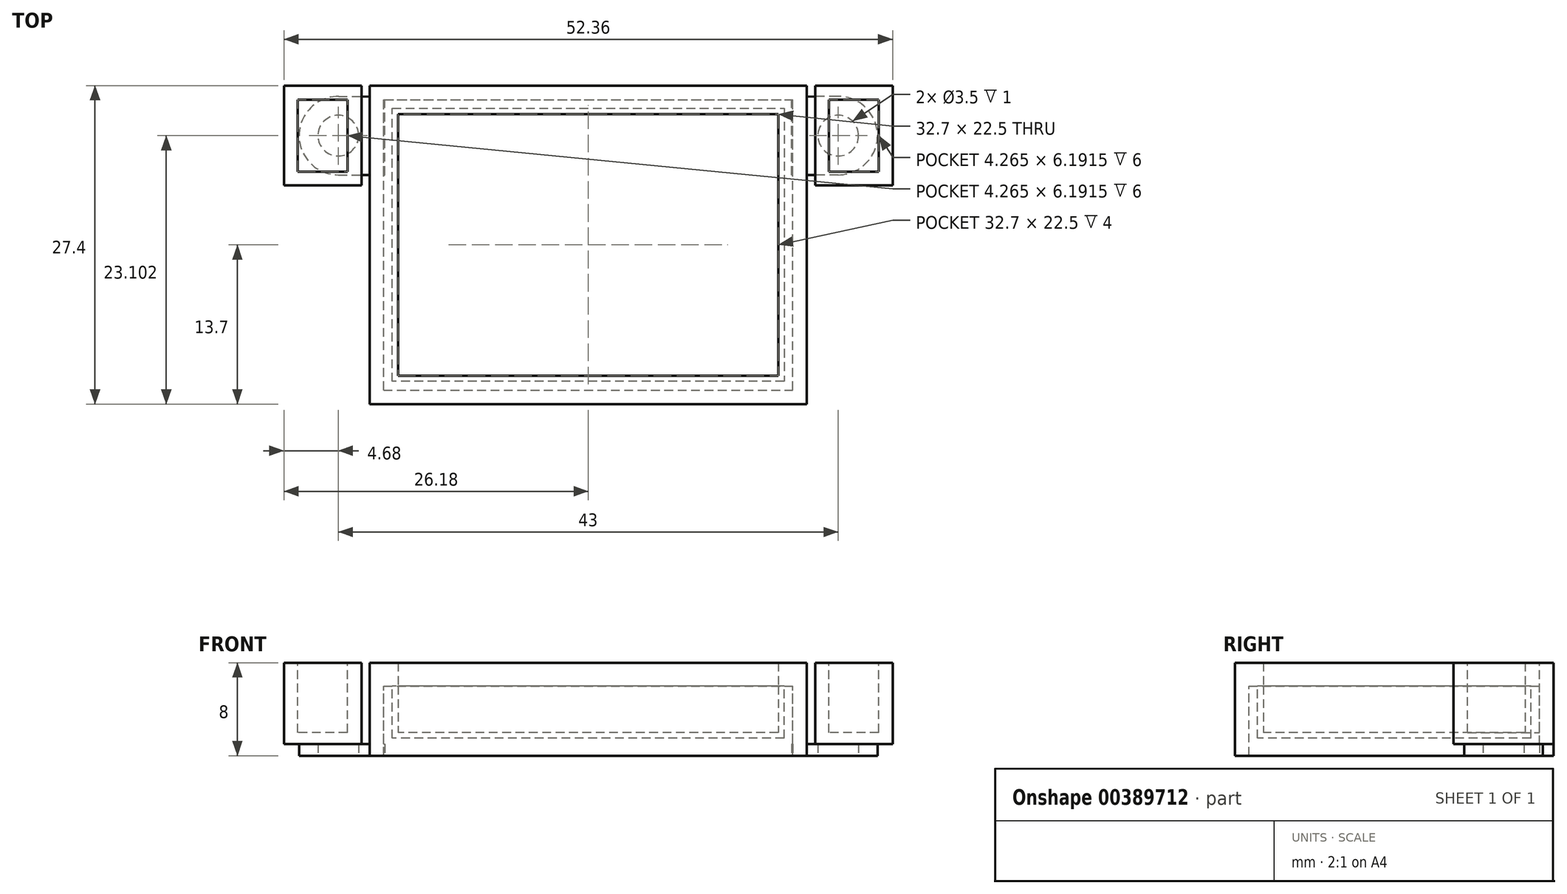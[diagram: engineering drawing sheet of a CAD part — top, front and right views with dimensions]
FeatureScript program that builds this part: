
annotation { "Feature Type Name" : "Feature", "Feature Type Description" : "" }
export const myFeature = defineFeature(function(context is Context, id is Id, definition is map)
    precondition{}
    {
        {
            var Q0;
            Q0=qCreatedBy(makeId("Top.planeOp"),FACE);
            var sketch = newSketch(context, id + "F0", { "sketchPlane" : qUnion([Q0])});
            skLineSegment(sketch, "E0.bottom", {"start": v(-15.2, 11.25) * mm, "end": v(-12.4, 11.25) * mm});
            skLineSegment(sketch, "E0.top", {"start": v(-15.2, -11.25) * mm, "end": v(-12.4, -11.25) * mm});
            skLineSegment(sketch, "E0.left", {"start": v(-15.2, 11.25) * mm, "end": v(-15.2, -11.25) * mm});
            skLineSegment(sketch, "E0.right", {"start": v(-12.4, 11.25) * mm, "end": v(-12.4, -11.25) * mm});
            skLineSegment(sketch, "E1", {"start": v(-42.25, 0) * mm, "end": v(42.25, 0) * mm, "construction": true});
            skLineSegment(sketch, "E2", {"start": v(0, 24.53) * mm, "end": v(0, -24.53) * mm, "construction": true});
            skLineSegment(sketch, "E3.MirrorCS", {"start": v(12.4, 11.25) * mm, "end": v(12.4, -11.25) * mm});
            skLineSegment(sketch, "E4.MirrorCS", {"start": v(15.2, -11.25) * mm, "end": v(12.4, -11.25) * mm});
            skLineSegment(sketch, "E5.MirrorCS", {"start": v(15.2, 11.25) * mm, "end": v(15.2, -11.25) * mm});
            skLineSegment(sketch, "E6.MirrorCS", {"start": v(15.2, 11.25) * mm, "end": v(12.4, 11.25) * mm});
            skLineSegment(sketch, "E7.bottom", {"start": v(-17.6, -12.5) * mm, "end": v(17.6, -12.5) * mm});
            skLineSegment(sketch, "E7.top", {"start": v(-17.6, 12.5) * mm, "end": v(17.6, 12.5) * mm});
            skLineSegment(sketch, "E7.left", {"start": v(-17.6, -12.5) * mm, "end": v(-17.6, 12.5) * mm});
            skLineSegment(sketch, "E7.right", {"start": v(17.6, -12.5) * mm, "end": v(17.6, 12.5) * mm});
            skLineSegment(sketch, "E8.0", {"start": v(-18.8, 13.7) * mm, "end": v(18.8, 13.7) * mm});
            skLineSegment(sketch, "E8.1", {"start": v(-18.8, -13.7) * mm, "end": v(-18.8, 13.7) * mm});
            skLineSegment(sketch, "E8.2", {"start": v(-18.8, -13.7) * mm, "end": v(18.8, -13.7) * mm});
            skLineSegment(sketch, "E8.3", {"start": v(18.8, -13.7) * mm, "end": v(18.8, 13.7) * mm});
            skLineSegment(sketch, "E9.bottom", {"start": v(-19.51, 13.7) * mm, "end": v(-26.18, 13.7) * mm});
            skLineSegment(sketch, "E9.top", {"start": v(-19.51, 5.1) * mm, "end": v(-26.18, 5.1) * mm});
            skLineSegment(sketch, "E9.left", {"start": v(-19.51, 13.7) * mm, "end": v(-19.51, 5.1) * mm});
            skLineSegment(sketch, "E9.right", {"start": v(-26.18, 13.7) * mm, "end": v(-26.18, 5.1) * mm});
            skLineSegment(sketch, "E10.MirrorCS", {"start": v(19.51, 13.7) * mm, "end": v(19.51, 5.1) * mm});
            skLineSegment(sketch, "E11.MirrorCS", {"start": v(19.51, 13.7) * mm, "end": v(26.18, 13.7) * mm});
            skLineSegment(sketch, "E12.MirrorCS", {"start": v(26.18, 13.7) * mm, "end": v(26.18, 5.1) * mm});
            skLineSegment(sketch, "E13.MirrorCS", {"start": v(19.51, 5.1) * mm, "end": v(26.18, 5.1) * mm});
            skSolve(sketch);
        }
        {
            var Q0;
            Q0 = qSketchRegion(id + "F0", true);
            var Q1;
            Q1=makeQuery(id+"F0.imprint","IMPRINT",FACE,{"disambiguationData":[TD([[makeQuery(id+"F0.imprint","IMPRINT",EDGE,{"derivedFrom":sQuery(id+"F0.wireOp",EDGE,"E0.bottom")}),1.0]])]});
            extrude(context, id + "F1", {"entities" : qUnion([Q0, Q1]), "depth" : 2 * mm});
        }
        {
            var Q0;
            Q0=makeQuery(id+"F0.imprint","IMPRINT",FACE,{"disambiguationData":[TD([[makeQuery(id+"F0.imprint","IMPRINT",EDGE,{"derivedFrom":sQuery(id+"F0.wireOp",EDGE,"E7.bottom")}),-1.0]])]});
            extrude(context, id + "F2", {"entities" : qUnion([Q0]), "operationType" : NewBodyOperationType.ADD, "oppositeDirection" : true, "depth" : 6 * mm});
        }
        {
            var Q0;
            Q0=makeQuery(id+"F2.opExtrude","CAP_FACE",FACE,{"disambiguationData":[OSD([sQuery(id+"F0.wireOp",EDGE,"E7.bottom"),sQuery(id+"F0.wireOp",EDGE,"E7.top"),sQuery(id+"F0.wireOp",EDGE,"E7.left"),sQuery(id+"F0.wireOp",EDGE,"E7.right"),sQuery(id+"F0.wireOp",EDGE,"E8.0"),sQuery(id+"F0.wireOp",EDGE,"E8.1"),sQuery(id+"F0.wireOp",EDGE,"E8.2"),sQuery(id+"F0.wireOp",EDGE,"E8.3")])],"isStart":false});
            var sketch = newSketch(context, id + "F3", { "sketchPlane" : qUnion([Q0])});
            skLineSegment(sketch, "E14.0", {"start": v(-17.5, -12.75) * mm, "end": v(17.5, -12.75) * mm, "construction": true});
            skCircle(sketch, "E15", {"center": v(-21.5, -9.4) * mm, "radius": 1.75 * mm});
            skLineSegment(sketch, "E16.0", {"start": v(-17.5, 12.25) * mm, "end": v(-17.5, -12.75) * mm});
            skLineSegment(sketch, "E17", {"start": v(-21.5, -6.03) * mm, "end": v(-17.5, -6.03) * mm});
            skLineSegment(sketch, "E18", {"start": v(-17.5, -6.03) * mm, "end": v(-17.5, -12.75) * mm});
            skLineSegment(sketch, "E19", {"start": v(-21.48, -12.78) * mm, "end": v(-17.5, -12.75) * mm});
            skArc(sketch, "E20", {"start": v(-21.5, -6.03) * mm, "mid": v(-24.87, -9.61) * mm, "end": v(-21.08, -12.75) * mm});
            skArc(sketch, "E21", {"start": v(-21.08, -12.75) * mm, "mid": v(-18.13, -9.2) * mm, "end": v(-21.5, -6.03) * mm, "construction": true});
            skLineSegment(sketch, "E22", {"start": v(0, -19.53) * mm, "end": v(0, 18.18) * mm, "construction": true});
            skPoint(sketch, "E22.endSnap0", {"position": v(0, -12.75) * mm});
            skLineSegment(sketch, "E23.MirrorCS", {"start": v(21.5, -6.03) * mm, "end": v(17.5, -6.03) * mm});
            skArc(sketch, "E24.MirrorCS", {"start": v(21.5, -6.03) * mm, "mid": v(24.87, -9.61) * mm, "end": v(21.08, -12.75) * mm});
            skLineSegment(sketch, "E25.MirrorCS", {"start": v(21.48, -12.78) * mm, "end": v(17.5, -12.75) * mm});
            skLineSegment(sketch, "E26.MirrorCS", {"start": v(17.5, -6.03) * mm, "end": v(17.5, -12.75) * mm});
            skCircle(sketch, "E27.MirrorC", {"center": v(21.5, -9.4) * mm, "radius": 1.75 * mm});
            skSolve(sketch);
        }
        {
            var Q0;
            Q0 = qSketchRegion(id + "F3", true);
            extrude(context, id + "F4", {"entities" : qUnion([Q0]), "operationType" : NewBodyOperationType.ADD, "oppositeDirection" : true, "depth" : 1 * mm});
        }
        {
            var Q0;
            Q0=makeQuery(id+"F1.opExtrude","CAP_FACE",FACE,{"disambiguationData":[OSD([sQuery(id+"F0.wireOp",EDGE,"E9.bottom"),sQuery(id+"F0.wireOp",EDGE,"E9.top"),sQuery(id+"F0.wireOp",EDGE,"E9.left"),sQuery(id+"F0.wireOp",EDGE,"E9.right")])],"isStart":true});
            var Q1;
            Q1=makeQuery(id+"F1.opExtrude","CAP_FACE",FACE,{"disambiguationData":[OSD([sQuery(id+"F0.wireOp",EDGE,"E10.MirrorCS"),sQuery(id+"F0.wireOp",EDGE,"E11.MirrorCS"),sQuery(id+"F0.wireOp",EDGE,"E12.MirrorCS"),sQuery(id+"F0.wireOp",EDGE,"E13.MirrorCS")])],"isStart":true});
            extrude(context, id + "F5", {"entities" : qUnion([Q0, Q1]), "operationType" : NewBodyOperationType.ADD, "depth" : 5 * mm});
        }
        {
            var Q0;
            Q0=makeQuery(id+"F1.opExtrude","CAP_FACE",FACE,{"disambiguationData":[OSD([sQuery(id+"F0.wireOp",EDGE,"E9.bottom"),sQuery(id+"F0.wireOp",EDGE,"E9.top"),sQuery(id+"F0.wireOp",EDGE,"E9.left"),sQuery(id+"F0.wireOp",EDGE,"E9.right")])],"isStart":false});
            var sketch = newSketch(context, id + "F6", { "sketchPlane" : qUnion([Q0])});
            skLineSegment(sketch, "E28.0.0", {"start": v(19.51, 13.7) * mm, "end": v(19.51, 5.1) * mm, "construction": true});
            skLineSegment(sketch, "E28.0.1", {"start": v(19.51, 5.1) * mm, "end": v(26.18, 5.1) * mm, "construction": true});
            skLineSegment(sketch, "E28.0.2", {"start": v(26.18, 5.1) * mm, "end": v(26.18, 13.7) * mm, "construction": true});
            skLineSegment(sketch, "E28.0.3", {"start": v(26.18, 13.7) * mm, "end": v(19.51, 13.7) * mm, "construction": true});
            skLineSegment(sketch, "E29.0", {"start": v(-19.51, 5.1) * mm, "end": v(-26.18, 5.1) * mm, "construction": true});
            skLineSegment(sketch, "E29.1", {"start": v(-26.18, 13.7) * mm, "end": v(-26.18, 5.1) * mm, "construction": true});
            skLineSegment(sketch, "E29.2", {"start": v(-19.51, 13.7) * mm, "end": v(-26.18, 13.7) * mm, "construction": true});
            skLineSegment(sketch, "E29.3", {"start": v(-19.51, 13.7) * mm, "end": v(-19.51, 5.1) * mm, "construction": true});
            skLineSegment(sketch, "E30.0", {"start": v(-20.71, 12.5) * mm, "end": v(-24.98, 12.5) * mm});
            skLineSegment(sketch, "E30.1", {"start": v(-20.71, 12.5) * mm, "end": v(-20.71, 6.3) * mm});
            skLineSegment(sketch, "E30.2", {"start": v(-20.71, 6.3) * mm, "end": v(-24.98, 6.3) * mm});
            skLineSegment(sketch, "E30.3", {"start": v(-24.98, 12.5) * mm, "end": v(-24.98, 6.3) * mm});
            skLineSegment(sketch, "E31.0", {"start": v(24.98, 12.5) * mm, "end": v(20.71, 12.5) * mm});
            skLineSegment(sketch, "E31.1", {"start": v(24.98, 6.3) * mm, "end": v(24.98, 12.5) * mm});
            skLineSegment(sketch, "E31.2", {"start": v(20.71, 6.3) * mm, "end": v(24.98, 6.3) * mm});
            skLineSegment(sketch, "E31.3", {"start": v(20.71, 12.5) * mm, "end": v(20.71, 6.3) * mm});
            skSolve(sketch);
        }
        {
            var Q0;
            Q0=makeQuery(id+"F6.imprint","IMPRINT",FACE,{"disambiguationData":[TD([[makeQuery(id+"F6.imprint","IMPRINT",EDGE,{"derivedFrom":sQuery(id+"F6.wireOp",EDGE,"E30.0")}),1.0]])]});
            var Q1;
            Q1=makeQuery(id+"F6.imprint","IMPRINT",FACE,{"disambiguationData":[TD([[makeQuery(id+"F6.imprint","IMPRINT",EDGE,{"derivedFrom":sQuery(id+"F6.wireOp",EDGE,"E31.0")}),1.0]])]});
            extrude(context, id + "F7", {"entities" : qUnion([Q0, Q1]), "operationType" : NewBodyOperationType.REMOVE, "oppositeDirection" : true, "depth" : 6 * mm});
        }
        {
            var Q0;
            Q0=makeQuery(id+"F1.opExtrude","CAP_FACE",FACE,{"disambiguationData":[OSD([sQuery(id+"F0.wireOp",EDGE,"E0.bottom"),sQuery(id+"F0.wireOp",EDGE,"E0.top"),sQuery(id+"F0.wireOp",EDGE,"E0.left"),sQuery(id+"F0.wireOp",EDGE,"E0.right"),sQuery(id+"F0.wireOp",EDGE,"E3.MirrorCS"),sQuery(id+"F0.wireOp",EDGE,"E4.MirrorCS"),sQuery(id+"F0.wireOp",EDGE,"E5.MirrorCS"),sQuery(id+"F0.wireOp",EDGE,"E6.MirrorCS"),sQuery(id+"F0.wireOp",EDGE,"E7.bottom"),sQuery(id+"F0.wireOp",EDGE,"E7.top"),sQuery(id+"F0.wireOp",EDGE,"E7.left"),sQuery(id+"F0.wireOp",EDGE,"E7.right")])],"isStart":true});
            cPlane(context, id + "F8", {"entities" : qUnion([Q0]), "cplaneType" : CPlaneType.OFFSET, "offset" : 0 * mm, "width" : 150 * mm, "height" : 150 * mm});
        }
        {
            var Q0;
            Q0=qCreatedBy(id+"F8.planeOp",FACE);
            var sketch = newSketch(context, id + "F9", { "sketchPlane" : qUnion([Q0])});
            skLineSegment(sketch, "E32.0.0", {"start": v(-17.6, -12.5) * mm, "end": v(17.6, -12.5) * mm});
            skLineSegment(sketch, "E32.0.1", {"start": v(17.6, -12.5) * mm, "end": v(17.6, 12.5) * mm});
            skLineSegment(sketch, "E32.0.2", {"start": v(17.6, 12.5) * mm, "end": v(-17.6, 12.5) * mm});
            skLineSegment(sketch, "E32.0.3", {"start": v(-17.6, 12.5) * mm, "end": v(-17.6, -12.5) * mm});
            skLineSegment(sketch, "E33.0", {"start": v(16.85, 11.75) * mm, "end": v(-16.85, 11.75) * mm});
            skLineSegment(sketch, "E33.1", {"start": v(16.85, -11.75) * mm, "end": v(16.85, 11.75) * mm});
            skLineSegment(sketch, "E33.2", {"start": v(-16.85, -11.75) * mm, "end": v(16.85, -11.75) * mm});
            skLineSegment(sketch, "E33.3", {"start": v(-16.85, 11.75) * mm, "end": v(-16.85, -11.75) * mm});
            skLineSegment(sketch, "E34.0", {"start": v(16.35, 11.25) * mm, "end": v(-16.35, 11.25) * mm});
            skLineSegment(sketch, "E34.1", {"start": v(16.35, -11.25) * mm, "end": v(16.35, 11.25) * mm});
            skLineSegment(sketch, "E34.2", {"start": v(-16.35, -11.25) * mm, "end": v(16.35, -11.25) * mm});
            skLineSegment(sketch, "E34.3", {"start": v(-16.35, 11.25) * mm, "end": v(-16.35, -11.25) * mm});
            skPoint(sketch, "E35.0", {"position": v(-17.6, -12.5) * mm});
            skPoint(sketch, "E35.1", {"position": v(-17.6, 12.5) * mm});
            skPoint(sketch, "E35.2", {"position": v(17.6, 12.5) * mm});
            skPoint(sketch, "E35.3", {"position": v(17.6, -12.5) * mm});
            skSolve(sketch);
        }
        {
            var Q0;
            Q0=makeQuery(id+"F9.imprint","IMPRINT",FACE,{"disambiguationData":[TD([[makeQuery(id+"F9.imprint","IMPRINT",EDGE,{"derivedFrom":sQuery(id+"F9.wireOp",EDGE,"E33.0")}),1.0]])]});
            var Q1;
            Q1=makeQuery(id+"F9.imprint","IMPRINT",FACE,{"disambiguationData":[TD([[makeQuery(id+"F9.imprint","IMPRINT",EDGE,{"derivedFrom":sQuery(id+"F9.wireOp",EDGE,"E34.0")}),1.0]])]});
            extrude(context, id + "F10", {"entities" : qUnion([Q0, Q1]), "depth" : 4.5 * mm});
        }
        {
            var Q0;
            Q0=makeQuery(id+"F9.imprint","IMPRINT",FACE,{"disambiguationData":[TD([[makeQuery(id+"F9.imprint","IMPRINT",EDGE,{"derivedFrom":sQuery(id+"F9.wireOp",EDGE,"E34.0")}),1.0]])]});
            extrude(context, id + "F11", {"entities" : qUnion([Q0]), "operationType" : NewBodyOperationType.REMOVE, "oppositeDirection" : true, "depth" : 4.5 * mm, "hasSecondDirection" : true, "secondDirectionOppositeDirection" : false, "secondDirectionDepth" : 4 * mm});
        }
    });
